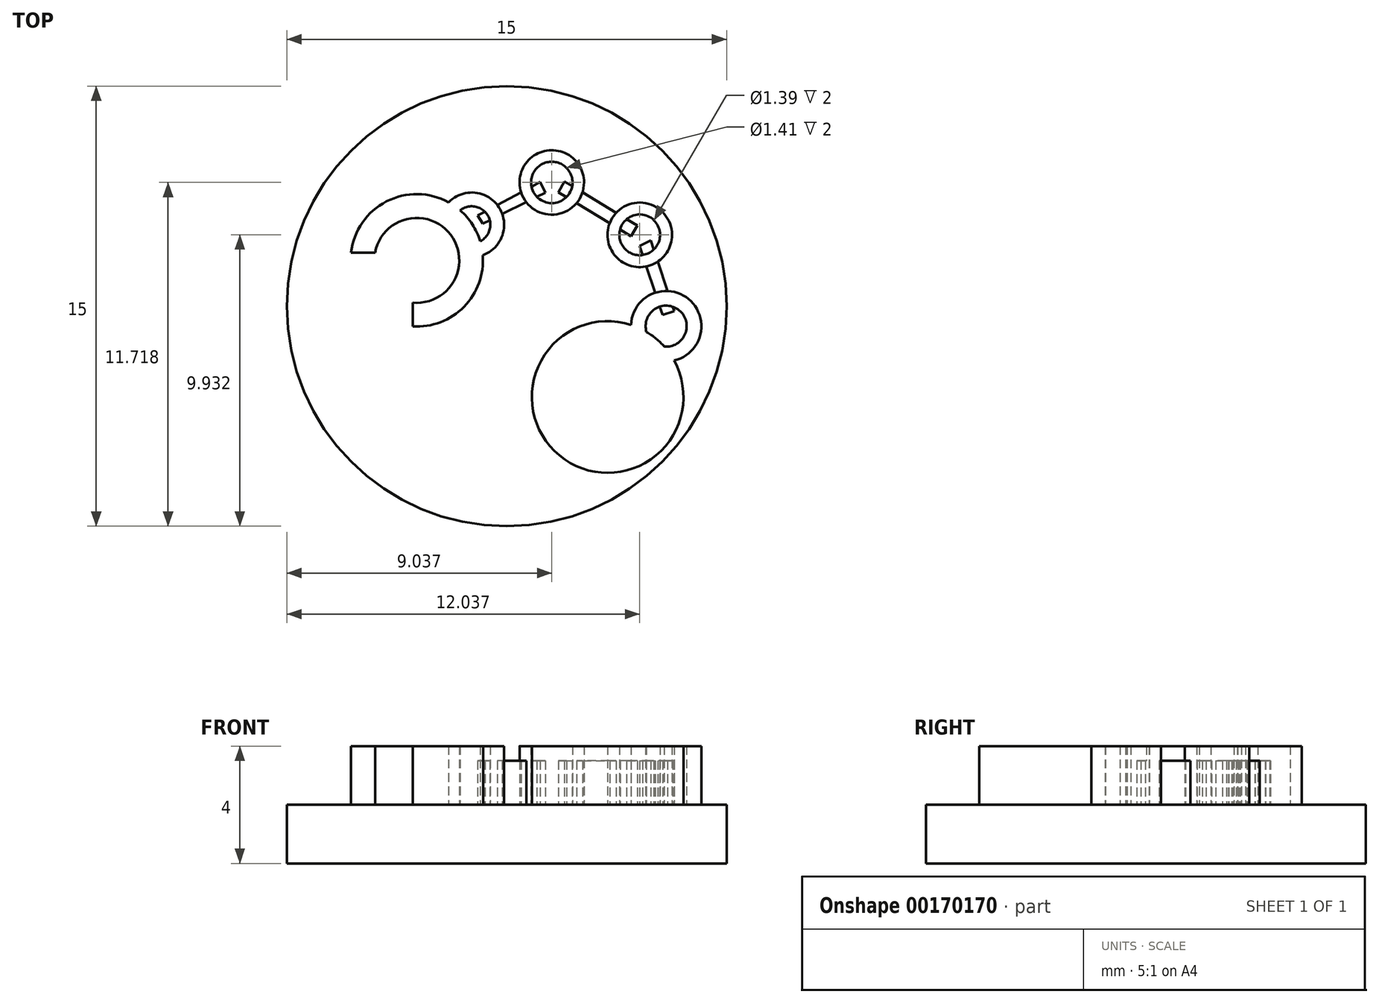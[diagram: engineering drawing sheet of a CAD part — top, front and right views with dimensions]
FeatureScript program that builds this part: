
annotation { "Feature Type Name" : "Feature", "Feature Type Description" : "" }
export const myFeature = defineFeature(function(context is Context, id is Id, definition is map)
    precondition{}
    {
        {
            var Q0;
            Q0=qCreatedBy(makeId("Top.planeOp"),FACE);
            var sketch = newSketch(context, id + "F0", { "sketchPlane" : qUnion([Q0])});
            skCircle(sketch, "E0", {"center": v(0, 0) * mm, "radius": 7.5 * mm});
            skSolve(sketch);
        }
        {
            var Q0;
            Q0 = qSketchRegion(id + "F0", true);
            extrude(context, id + "F1", {"entities" : qUnion([Q0]), "depth" : 2 * mm});
        }
        {
            var Q0;
            Q0=makeQuery(id+"F1.opExtrude","CAP_FACE",FACE,{"disambiguationData":[OSD([sQuery(id+"F0.wireOp",EDGE,"E0")])],"isStart":false});
            var sketch = newSketch(context, id + "F2", { "sketchPlane" : qUnion([Q0])});
            skArc(sketch, "E1", {"start": v(4.24, -0.64) * mm, "mid": v(1.8, -5.1) * mm, "end": v(5.7, -1.85) * mm});
            skCircle(sketch, "E2", {"center": v(1.54, 4.22) * mm, "radius": 1.1 * mm});
            skCircle(sketch, "E3", {"center": v(4.54, 2.43) * mm, "radius": 1.1 * mm});
            skArc(sketch, "E4", {"start": v(5.7, -1.85) * mm, "mid": v(6.2, 0.24) * mm, "end": v(4.24, -0.64) * mm});
            skLineSegment(sketch, "E5", {"start": v(-1.91, 3.63) * mm, "end": v(-1.91, 3.63) * mm});
            skCircle(sketch, "E6", {"center": v(1.54, 4.22) * mm, "radius": 0.7 * mm});
            skCircle(sketch, "E7", {"center": v(4.54, 2.43) * mm, "radius": 0.7 * mm});
            skArc(sketch, "E8", {"start": v(5.38, -1.38) * mm, "mid": v(5.88, -0.14) * mm, "end": v(4.77, -0.88) * mm});
            skArc(sketch, "E9.trimOffspring", {"start": v(5.38, -1.38) * mm, "mid": v(5.1, -1.1) * mm, "end": v(4.77, -0.88) * mm});
            skArc(sketch, "E10", {"start": v(-3.2, -0.7) * mm, "mid": v(-1.46, -0.02) * mm, "end": v(-0.81, 1.74) * mm});
            skArc(sketch, "E11", {"start": v(-0.81, 1.74) * mm, "mid": v(-0.26, 3.37) * mm, "end": v(-1.98, 3.54) * mm});
            skArc(sketch, "E12", {"start": v(-3.2, 0.12) * mm, "mid": v(-1.9, 2.43) * mm, "end": v(-4.49, 1.83) * mm});
            skArc(sketch, "E13", {"start": v(-0.9, 2.21) * mm, "mid": v(-0.66, 3.12) * mm, "end": v(-1.58, 3.27) * mm});
            skLineSegment(sketch, "E14", {"start": v(-5.3, 1.83) * mm, "end": v(-4.49, 1.83) * mm});
            skLineSegment(sketch, "E15", {"start": v(-3.2, 0.12) * mm, "end": v(-3.2, -0.7) * mm});
            skArc(sketch, "E16.trimOffspring", {"start": v(-0.9, 2.21) * mm, "mid": v(-1.17, 2.79) * mm, "end": v(-1.58, 3.27) * mm});
            skArc(sketch, "E17.trimOffspring", {"start": v(-1.98, 3.54) * mm, "mid": v(-4.1, 3.57) * mm, "end": v(-5.3, 1.83) * mm});
            skSolve(sketch);
        }
        {
            var Q0;
            Q0 = qSketchRegion(id + "F2", true);
            extrude(context, id + "F3", {"entities" : qUnion([Q0]), "operationType" : NewBodyOperationType.ADD, "depth" : 2 * mm});
        }
        {
            var Q0;
            {var subQ0=sQuery(id+"F0.wireOp",EDGE,"E0");Q0=makeQuery(id+"F3.boolean.opBoolean","SPLIT",FACE,{"disambiguationData":[TD([makeQuery(id+"F1.opExtrude","SWEPT_FACE",FACE,{"disambiguationData":[OSD([subQ0])]})])],"derivedFrom":makeQuery(id+"F1.opExtrude","CAP_FACE",FACE,{"disambiguationData":[OSD([subQ0])],"isStart":false})});}
            var sketch = newSketch(context, id + "F4", { "sketchPlane" : qUnion([Q0])});
            skLineSegment(sketch, "E18", {"start": v(-1, 3.09) * mm, "end": v(-0.81, 2.81) * mm});
            skLineSegment(sketch, "E19", {"start": v(-0.81, 2.81) * mm, "end": v(1.32, 3.87) * mm});
            skLineSegment(sketch, "E20", {"start": v(1.32, 3.87) * mm, "end": v(1.14, 4.23) * mm});
            skLineSegment(sketch, "E21", {"start": v(1.14, 4.23) * mm, "end": v(-1, 3.09) * mm});
            skLineSegment(sketch, "E22", {"start": v(1.97, 4.25) * mm, "end": v(4.46, 2.75) * mm});
            skLineSegment(sketch, "E23", {"start": v(4.46, 2.75) * mm, "end": v(4.24, 2.39) * mm});
            skLineSegment(sketch, "E24", {"start": v(4.24, 2.39) * mm, "end": v(1.77, 3.88) * mm});
            skLineSegment(sketch, "E25", {"start": v(1.77, 3.88) * mm, "end": v(1.97, 4.25) * mm});
            skLineSegment(sketch, "E26", {"start": v(4.53, 2.06) * mm, "end": v(5.31, -0.3) * mm});
            skLineSegment(sketch, "E27", {"start": v(5.31, -0.3) * mm, "end": v(5.7, -0.17) * mm});
            skLineSegment(sketch, "E28", {"start": v(5.7, -0.17) * mm, "end": v(4.9, 2.24) * mm});
            skLineSegment(sketch, "E29", {"start": v(4.9, 2.24) * mm, "end": v(4.53, 2.06) * mm});
            skSolve(sketch);
        }
        {
            var Q0;
            Q0 = qSketchRegion(id + "F4", true);
            extrude(context, id + "F5", {"entities" : qUnion([Q0]), "operationType" : NewBodyOperationType.ADD, "depth" : 1.5 * mm});
        }
    });
